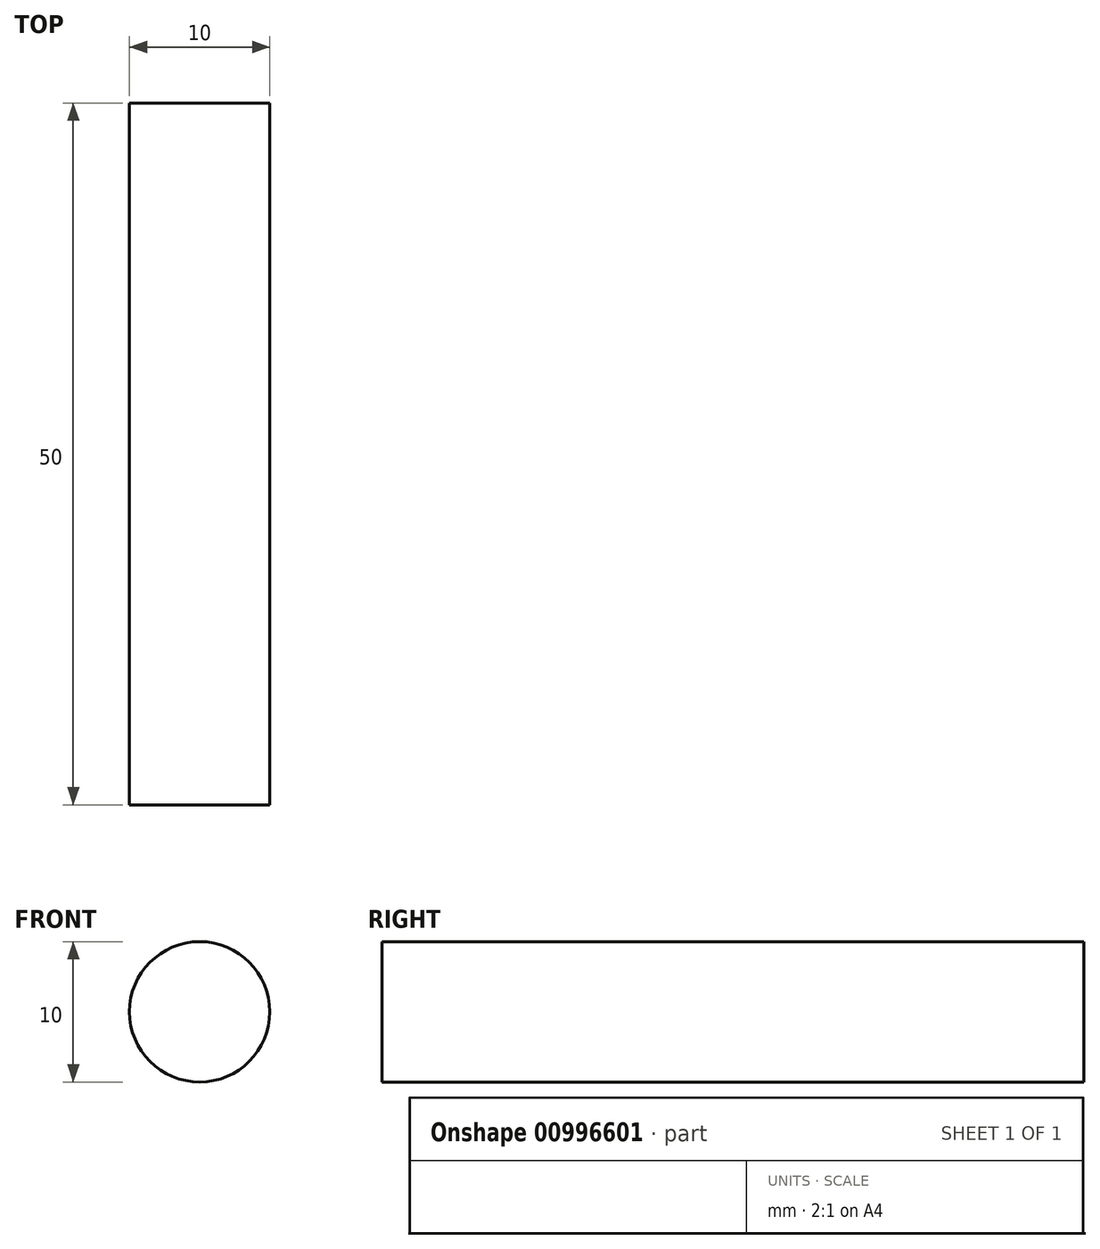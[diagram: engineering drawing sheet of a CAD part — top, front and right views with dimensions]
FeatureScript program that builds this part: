
annotation { "Feature Type Name" : "Feature", "Feature Type Description" : "" }
export const myFeature = defineFeature(function(context is Context, id is Id, definition is map)
    precondition{}
    {
        {
            var Q0;
            Q0=qCreatedBy(makeId("Front.planeOp"),FACE);
            var sketch = newSketch(context, id + "F0", { "sketchPlane" : qUnion([Q0])});
            skCircle(sketch, "E0", {"center": v(0, 0) * mm, "radius": 5 * mm});
            skSolve(sketch);
        }
        {
            var Q0;
            Q0 = qSketchRegion(id + "F0", true);
            extrude(context, id + "F1", {"entities" : qUnion([Q0]), "depth" : 50 * mm, "offsetDistance" : 25 * mm});
        }
    });
